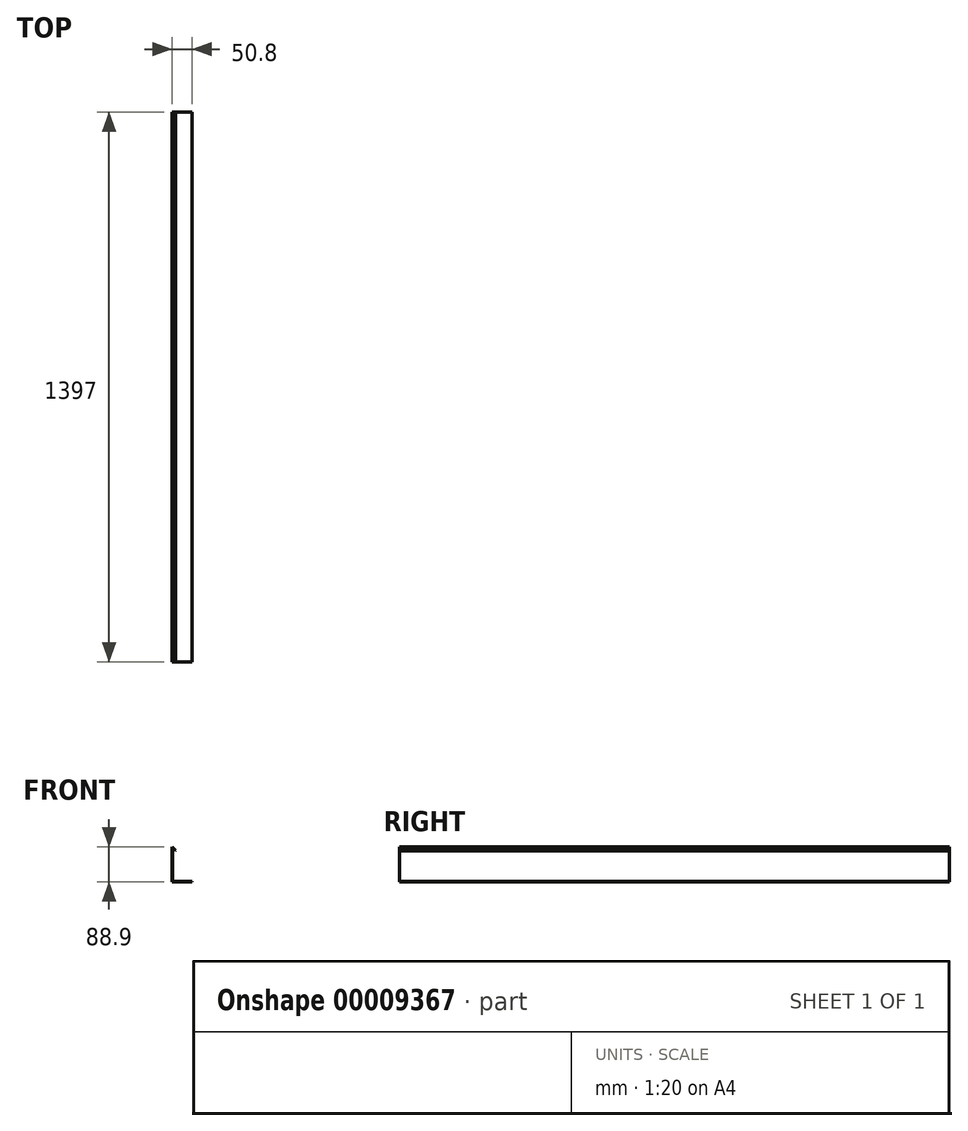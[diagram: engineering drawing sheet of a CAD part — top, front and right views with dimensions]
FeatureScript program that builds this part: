
annotation { "Feature Type Name" : "Feature", "Feature Type Description" : "" }
export const myFeature = defineFeature(function(context is Context, id is Id, definition is map)
    precondition{}
    {
        {
            var Q0;
            Q0=qCreatedBy(makeId("Front.planeOp"),FACE);
            var sketch = newSketch(context, id + "F0", { "sketchPlane" : qUnion([Q0])});
            skLineSegment(sketch, "E0", {"start": v(8.98, 79.92) * mm, "end": v(0, 88.9) * mm});
            skLineSegment(sketch, "E1", {"start": v(0, 88.9) * mm, "end": v(0, 0) * mm});
            skLineSegment(sketch, "E2", {"start": v(0, 0) * mm, "end": v(50.8, 0) * mm});
            skLineSegment(sketch, "E3", {"start": v(50.8, 0) * mm, "end": v(50.8, 1.31) * mm});
            skLineSegment(sketch, "E4", {"start": v(50.8, 1.31) * mm, "end": v(1.31, 1.31) * mm});
            skLineSegment(sketch, "E5", {"start": v(1.31, 1.31) * mm, "end": v(1.31, 85.74) * mm});
            skLineSegment(sketch, "E6", {"start": v(1.31, 85.74) * mm, "end": v(8.05, 79) * mm});
            skLineSegment(sketch, "E7", {"start": v(8.05, 79) * mm, "end": v(8.98, 79.92) * mm});
            skSolve(sketch);
        }
        {
            var Q0;
            Q0=makeQuery(id+"F0.imprint","IMPRINT",FACE,{"disambiguationData":[TD([[makeQuery(id+"F0.imprint","IMPRINT",EDGE,{"derivedFrom":sQuery(id+"F0.wireOp",EDGE,"E0")}),1.0]])]});
            extrude(context, id + "F1", {"entities" : qUnion([Q0]), "depth" : 1397 * mm});
        }
    });
